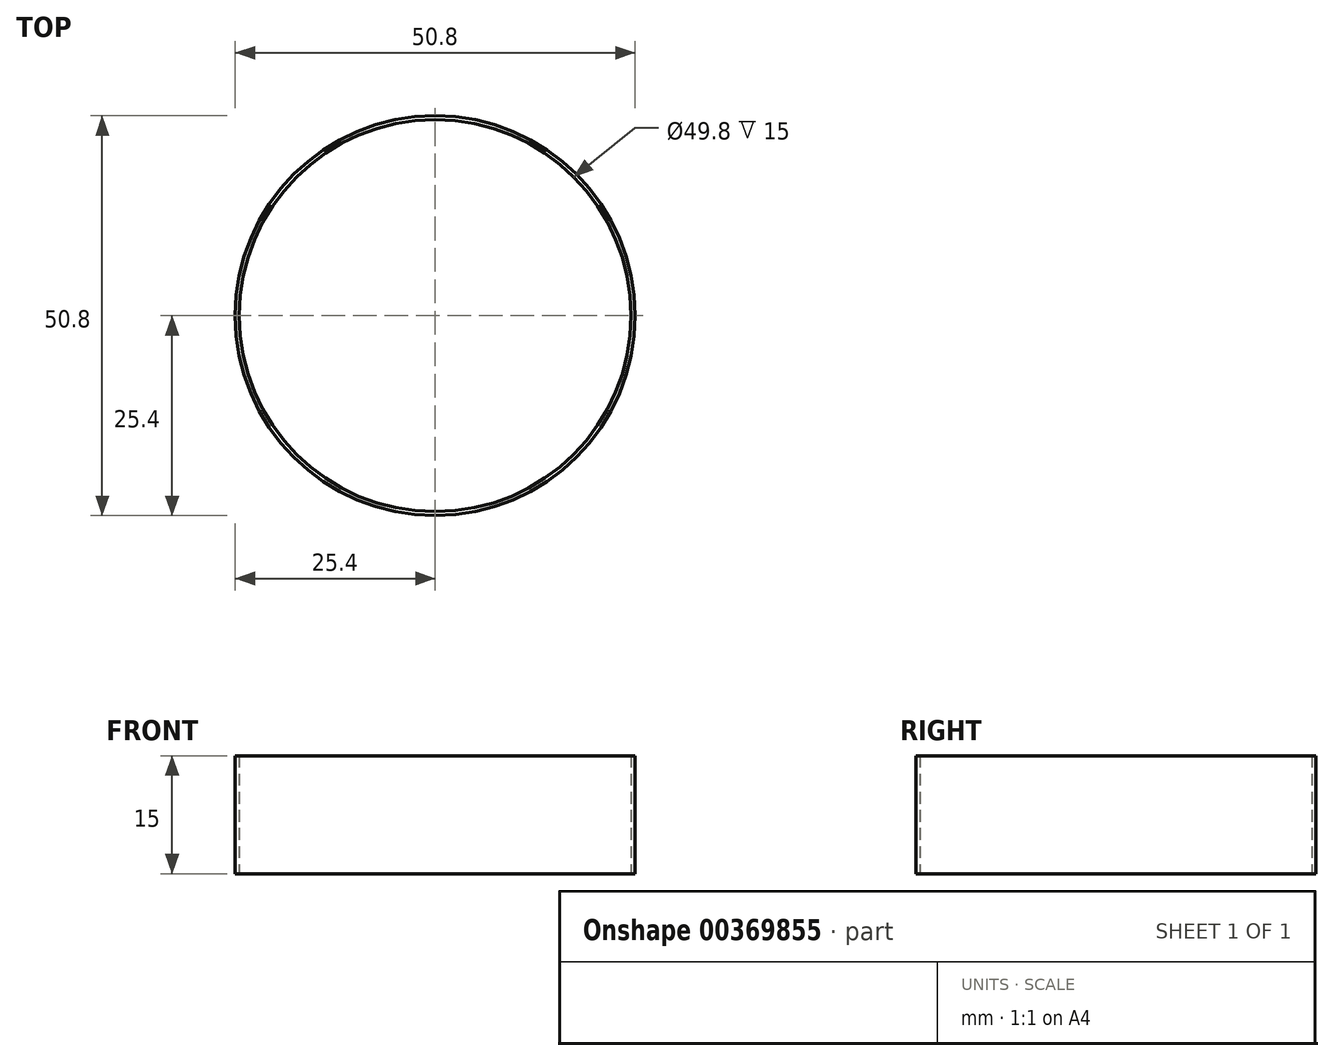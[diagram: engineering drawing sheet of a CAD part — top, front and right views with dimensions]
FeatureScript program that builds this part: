
annotation { "Feature Type Name" : "Feature", "Feature Type Description" : "" }
export const myFeature = defineFeature(function(context is Context, id is Id, definition is map)
    precondition{}
    {
        {
            var Q0;
            Q0=qCreatedBy(makeId("Top.planeOp"),FACE);
            var sketch = newSketch(context, id + "F0", { "sketchPlane" : qUnion([Q0])});
            skCircle(sketch, "E0", {"center": v(0, 0) * mm, "radius": 25.4 * mm});
            skCircle(sketch, "E1", {"center": v(0, 0) * mm, "radius": 24.9 * mm});
            skSolve(sketch);
        }
        {
            var Q0;
            Q0 = qSketchRegion(id + "F0", true);
            extrude(context, id + "F1", {"entities" : qUnion([Q0]), "depth" : 15 * mm});
        }
    });
